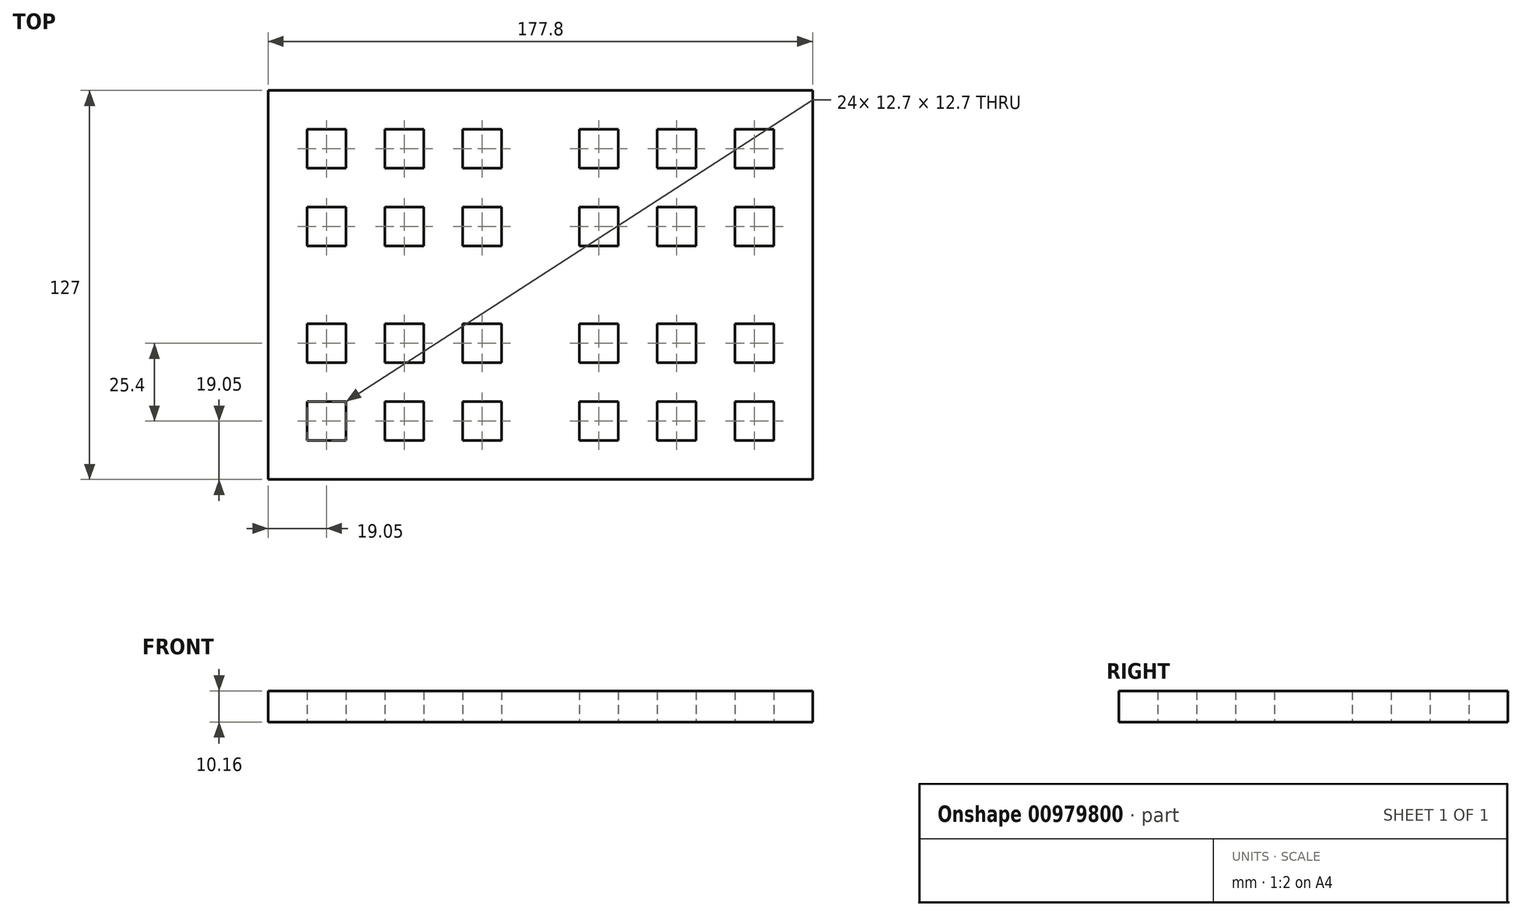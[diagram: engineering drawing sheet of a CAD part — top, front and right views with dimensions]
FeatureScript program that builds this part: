
annotation { "Feature Type Name" : "Feature", "Feature Type Description" : "" }
export const myFeature = defineFeature(function(context is Context, id is Id, definition is map)
    precondition{}
    {
        {
            var Q0;
            Q0=qCreatedBy(makeId("Top.planeOp"),FACE);
            var sketch = newSketch(context, id + "F0", { "sketchPlane" : qUnion([Q0])});
            skLineSegment(sketch, "E0.bottom", {"start": v(-88.9, 63.5) * mm, "end": v(88.9, 63.5) * mm});
            skLineSegment(sketch, "E0.top", {"start": v(-88.9, -63.5) * mm, "end": v(88.9, -63.5) * mm});
            skLineSegment(sketch, "E0.left", {"start": v(-88.9, 63.5) * mm, "end": v(-88.9, -63.5) * mm});
            skLineSegment(sketch, "E0.right", {"start": v(88.9, 63.5) * mm, "end": v(88.9, -63.5) * mm});
            skPoint(sketch, "E0.middle", {"position": v(0, 0) * mm});
            skLineSegment(sketch, "E1.bottom", {"start": v(-50.8, 50.8) * mm, "end": v(-38.1, 50.8) * mm});
            skLineSegment(sketch, "E1.top", {"start": v(-50.8, 38.1) * mm, "end": v(-38.1, 38.1) * mm});
            skLineSegment(sketch, "E1.left", {"start": v(-50.8, 50.8) * mm, "end": v(-50.8, 38.1) * mm});
            skLineSegment(sketch, "E2.2.0.0", {"start": v(-12.7, 50.8) * mm, "end": v(-12.7, 38.1) * mm});
            skLineSegment(sketch, "E2.2.0.1", {"start": v(-25.4, 50.8) * mm, "end": v(-12.7, 50.8) * mm});
            skLineSegment(sketch, "E2.2.0.2", {"start": v(-25.4, 38.1) * mm, "end": v(-12.7, 38.1) * mm});
            skLineSegment(sketch, "E3", {"start": v(-25.4, 50.8) * mm, "end": v(-25.4, 38.1) * mm});
            skLineSegment(sketch, "E4", {"start": v(-38.1, 50.8) * mm, "end": v(-38.1, 38.1) * mm});
            skLineSegment(sketch, "E5.0.1.0", {"start": v(-50.8, 25.4) * mm, "end": v(-38.1, 25.4) * mm});
            skLineSegment(sketch, "E5.0.1.1", {"start": v(-50.8, 25.4) * mm, "end": v(-50.8, 12.7) * mm});
            skLineSegment(sketch, "E5.0.1.2", {"start": v(-38.1, 25.4) * mm, "end": v(-38.1, 12.7) * mm});
            skLineSegment(sketch, "E5.0.1.3", {"start": v(-50.8, 12.7) * mm, "end": v(-38.1, 12.7) * mm});
            skLineSegment(sketch, "E5.0.1.4", {"start": v(-25.4, 25.4) * mm, "end": v(-25.4, 12.7) * mm});
            skLineSegment(sketch, "E5.0.1.5", {"start": v(-25.4, 12.7) * mm, "end": v(-12.7, 12.7) * mm});
            skLineSegment(sketch, "E5.0.1.6", {"start": v(-12.7, 25.4) * mm, "end": v(-12.7, 12.7) * mm});
            skLineSegment(sketch, "E5.0.1.7", {"start": v(-25.4, 25.4) * mm, "end": v(-12.7, 25.4) * mm});
            skLineSegment(sketch, "E5.1.1.4", {"start": v(-50.8, 25.4) * mm, "end": v(-50.8, 12.7) * mm});
            skLineSegment(sketch, "E5.1.1.5", {"start": v(-50.8, 12.7) * mm, "end": v(-38.1, 12.7) * mm});
            skLineSegment(sketch, "E5.1.1.6", {"start": v(-38.1, 25.4) * mm, "end": v(-38.1, 12.7) * mm});
            skLineSegment(sketch, "E5.1.1.7", {"start": v(-50.8, 25.4) * mm, "end": v(-38.1, 25.4) * mm});
            skLineSegment(sketch, "E6.0.1.0", {"start": v(-50.8, -12.7) * mm, "end": v(-38.1, -12.7) * mm});
            skLineSegment(sketch, "E6.0.1.1", {"start": v(-38.1, -12.7) * mm, "end": v(-38.1, -25.4) * mm});
            skLineSegment(sketch, "E6.0.1.2", {"start": v(-50.8, -25.4) * mm, "end": v(-38.1, -25.4) * mm});
            skLineSegment(sketch, "E6.0.1.3", {"start": v(-50.8, -12.7) * mm, "end": v(-50.8, -25.4) * mm});
            skLineSegment(sketch, "E6.0.1.4", {"start": v(-25.4, -12.7) * mm, "end": v(-25.4, -25.4) * mm});
            skLineSegment(sketch, "E6.0.1.5", {"start": v(-25.4, -12.7) * mm, "end": v(-12.7, -12.7) * mm});
            skLineSegment(sketch, "E6.0.1.6", {"start": v(-12.7, -12.7) * mm, "end": v(-12.7, -25.4) * mm});
            skLineSegment(sketch, "E6.0.1.7", {"start": v(-25.4, -25.4) * mm, "end": v(-12.7, -25.4) * mm});
            skLineSegment(sketch, "E6.0.1.8", {"start": v(-25.4, -38.1) * mm, "end": v(-12.7, -38.1) * mm});
            skLineSegment(sketch, "E6.0.1.9", {"start": v(-12.7, -38.1) * mm, "end": v(-12.7, -50.8) * mm});
            skLineSegment(sketch, "E6.0.1.10", {"start": v(-25.4, -50.8) * mm, "end": v(-12.7, -50.8) * mm});
            skLineSegment(sketch, "E6.0.1.11", {"start": v(-25.4, -38.1) * mm, "end": v(-25.4, -50.8) * mm});
            skLineSegment(sketch, "E6.0.1.12", {"start": v(-38.1, -38.1) * mm, "end": v(-38.1, -50.8) * mm});
            skLineSegment(sketch, "E6.0.1.13", {"start": v(-50.8, -50.8) * mm, "end": v(-38.1, -50.8) * mm});
            skLineSegment(sketch, "E6.0.1.14", {"start": v(-50.8, -38.1) * mm, "end": v(-50.8, -50.8) * mm});
            skLineSegment(sketch, "E6.0.1.15", {"start": v(-50.8, -38.1) * mm, "end": v(-38.1, -38.1) * mm});
            skLineSegment(sketch, "E6.1.0.0", {"start": v(12.7, 50.8) * mm, "end": v(25.4, 50.8) * mm});
            skLineSegment(sketch, "E6.1.0.1", {"start": v(25.4, 50.8) * mm, "end": v(25.4, 38.1) * mm});
            skLineSegment(sketch, "E6.1.0.2", {"start": v(12.7, 38.1) * mm, "end": v(25.4, 38.1) * mm});
            skLineSegment(sketch, "E6.1.0.3", {"start": v(12.7, 50.8) * mm, "end": v(12.7, 38.1) * mm});
            skLineSegment(sketch, "E6.1.0.4", {"start": v(38.1, 50.8) * mm, "end": v(38.1, 38.1) * mm});
            skLineSegment(sketch, "E6.1.0.5", {"start": v(38.1, 50.8) * mm, "end": v(50.8, 50.8) * mm});
            skLineSegment(sketch, "E6.1.0.6", {"start": v(50.8, 50.8) * mm, "end": v(50.8, 38.1) * mm});
            skLineSegment(sketch, "E6.1.0.7", {"start": v(38.1, 38.1) * mm, "end": v(50.8, 38.1) * mm});
            skLineSegment(sketch, "E6.1.0.8", {"start": v(38.1, 25.4) * mm, "end": v(50.8, 25.4) * mm});
            skLineSegment(sketch, "E6.1.0.9", {"start": v(50.8, 25.4) * mm, "end": v(50.8, 12.7) * mm});
            skLineSegment(sketch, "E6.1.0.10", {"start": v(38.1, 12.7) * mm, "end": v(50.8, 12.7) * mm});
            skLineSegment(sketch, "E6.1.0.11", {"start": v(38.1, 25.4) * mm, "end": v(38.1, 12.7) * mm});
            skLineSegment(sketch, "E6.1.0.12", {"start": v(25.4, 25.4) * mm, "end": v(25.4, 12.7) * mm});
            skLineSegment(sketch, "E6.1.0.13", {"start": v(12.7, 12.7) * mm, "end": v(25.4, 12.7) * mm});
            skLineSegment(sketch, "E6.1.0.14", {"start": v(12.7, 25.4) * mm, "end": v(12.7, 12.7) * mm});
            skLineSegment(sketch, "E6.1.0.15", {"start": v(12.7, 25.4) * mm, "end": v(25.4, 25.4) * mm});
            skLineSegment(sketch, "E6.1.1.0", {"start": v(12.7, -12.7) * mm, "end": v(25.4, -12.7) * mm});
            skLineSegment(sketch, "E6.1.1.1", {"start": v(25.4, -12.7) * mm, "end": v(25.4, -25.4) * mm});
            skLineSegment(sketch, "E6.1.1.2", {"start": v(12.7, -25.4) * mm, "end": v(25.4, -25.4) * mm});
            skLineSegment(sketch, "E6.1.1.3", {"start": v(12.7, -12.7) * mm, "end": v(12.7, -25.4) * mm});
            skLineSegment(sketch, "E6.1.1.4", {"start": v(38.1, -12.7) * mm, "end": v(38.1, -25.4) * mm});
            skLineSegment(sketch, "E6.1.1.5", {"start": v(38.1, -12.7) * mm, "end": v(50.8, -12.7) * mm});
            skLineSegment(sketch, "E6.1.1.6", {"start": v(50.8, -12.7) * mm, "end": v(50.8, -25.4) * mm});
            skLineSegment(sketch, "E6.1.1.7", {"start": v(38.1, -25.4) * mm, "end": v(50.8, -25.4) * mm});
            skLineSegment(sketch, "E6.1.1.8", {"start": v(38.1, -38.1) * mm, "end": v(50.8, -38.1) * mm});
            skLineSegment(sketch, "E6.1.1.9", {"start": v(50.8, -38.1) * mm, "end": v(50.8, -50.8) * mm});
            skLineSegment(sketch, "E6.1.1.10", {"start": v(38.1, -50.8) * mm, "end": v(50.8, -50.8) * mm});
            skLineSegment(sketch, "E6.1.1.11", {"start": v(38.1, -38.1) * mm, "end": v(38.1, -50.8) * mm});
            skLineSegment(sketch, "E6.1.1.12", {"start": v(25.4, -38.1) * mm, "end": v(25.4, -50.8) * mm});
            skLineSegment(sketch, "E6.1.1.13", {"start": v(12.7, -50.8) * mm, "end": v(25.4, -50.8) * mm});
            skLineSegment(sketch, "E6.1.1.14", {"start": v(12.7, -38.1) * mm, "end": v(12.7, -50.8) * mm});
            skLineSegment(sketch, "E6.1.1.15", {"start": v(12.7, -38.1) * mm, "end": v(25.4, -38.1) * mm});
            skLineSegment(sketch, "E7.1.0.0", {"start": v(-76.2, 12.7) * mm, "end": v(-63.5, 12.7) * mm});
            skLineSegment(sketch, "E7.1.0.1", {"start": v(-76.2, 25.4) * mm, "end": v(-76.2, 12.7) * mm});
            skLineSegment(sketch, "E7.1.0.2", {"start": v(-63.5, 25.4) * mm, "end": v(-63.5, 12.7) * mm});
            skLineSegment(sketch, "E7.1.0.3", {"start": v(-76.2, 50.8) * mm, "end": v(-63.5, 50.8) * mm});
            skLineSegment(sketch, "E7.1.0.4", {"start": v(-76.2, 50.8) * mm, "end": v(-76.2, 38.1) * mm});
            skLineSegment(sketch, "E7.1.0.5", {"start": v(-63.5, 50.8) * mm, "end": v(-63.5, 38.1) * mm});
            skLineSegment(sketch, "E7.1.0.6", {"start": v(-76.2, 38.1) * mm, "end": v(-63.5, 38.1) * mm});
            skLineSegment(sketch, "E7.1.0.7", {"start": v(-76.2, 25.4) * mm, "end": v(-63.5, 25.4) * mm});
            skLineSegment(sketch, "E7.1.0.8", {"start": v(-76.2, 12.7) * mm, "end": v(-63.5, 12.7) * mm});
            skLineSegment(sketch, "E7.1.0.9", {"start": v(-76.2, 50.8) * mm, "end": v(-63.5, 50.8) * mm});
            skLineSegment(sketch, "E7.1.0.10", {"start": v(-76.2, 38.1) * mm, "end": v(-63.5, 38.1) * mm});
            skLineSegment(sketch, "E7.1.0.11", {"start": v(-76.2, 50.8) * mm, "end": v(-76.2, 38.1) * mm});
            skLineSegment(sketch, "E7.1.0.12", {"start": v(-63.5, 25.4) * mm, "end": v(-63.5, 12.7) * mm});
            skLineSegment(sketch, "E7.1.0.13", {"start": v(-76.2, 25.4) * mm, "end": v(-76.2, 12.7) * mm});
            skLineSegment(sketch, "E7.1.0.14", {"start": v(-63.5, 50.8) * mm, "end": v(-63.5, 38.1) * mm});
            skLineSegment(sketch, "E7.1.0.15", {"start": v(-76.2, 25.4) * mm, "end": v(-63.5, 25.4) * mm});
            skLineSegment(sketch, "E8.1.0.0", {"start": v(-76.2, -50.8) * mm, "end": v(-63.5, -50.8) * mm});
            skLineSegment(sketch, "E8.1.0.1", {"start": v(-76.2, -38.1) * mm, "end": v(-76.2, -50.8) * mm});
            skLineSegment(sketch, "E8.1.0.2", {"start": v(-63.5, -38.1) * mm, "end": v(-63.5, -50.8) * mm});
            skLineSegment(sketch, "E8.1.0.3", {"start": v(-76.2, -12.7) * mm, "end": v(-63.5, -12.7) * mm});
            skLineSegment(sketch, "E8.1.0.4", {"start": v(-76.2, -12.7) * mm, "end": v(-76.2, -25.4) * mm});
            skLineSegment(sketch, "E8.1.0.5", {"start": v(-63.5, -12.7) * mm, "end": v(-63.5, -25.4) * mm});
            skLineSegment(sketch, "E8.1.0.6", {"start": v(-76.2, -25.4) * mm, "end": v(-63.5, -25.4) * mm});
            skLineSegment(sketch, "E8.1.0.7", {"start": v(-76.2, -38.1) * mm, "end": v(-63.5, -38.1) * mm});
            skLineSegment(sketch, "E8.1.0.8", {"start": v(-76.2, -50.8) * mm, "end": v(-63.5, -50.8) * mm});
            skLineSegment(sketch, "E8.1.0.9", {"start": v(-76.2, -12.7) * mm, "end": v(-63.5, -12.7) * mm});
            skLineSegment(sketch, "E8.1.0.10", {"start": v(-76.2, -25.4) * mm, "end": v(-63.5, -25.4) * mm});
            skLineSegment(sketch, "E8.1.0.11", {"start": v(-76.2, -12.7) * mm, "end": v(-76.2, -25.4) * mm});
            skLineSegment(sketch, "E8.1.0.12", {"start": v(-63.5, -38.1) * mm, "end": v(-63.5, -50.8) * mm});
            skLineSegment(sketch, "E8.1.0.13", {"start": v(-76.2, -38.1) * mm, "end": v(-76.2, -50.8) * mm});
            skLineSegment(sketch, "E8.1.0.14", {"start": v(-63.5, -12.7) * mm, "end": v(-63.5, -25.4) * mm});
            skLineSegment(sketch, "E8.1.0.15", {"start": v(-76.2, -38.1) * mm, "end": v(-63.5, -38.1) * mm});
            skLineSegment(sketch, "E9.1.0.4", {"start": v(63.52, 50.8) * mm, "end": v(63.52, 38.1) * mm});
            skLineSegment(sketch, "E9.1.0.5", {"start": v(63.52, 50.8) * mm, "end": v(76.22, 50.8) * mm});
            skLineSegment(sketch, "E9.1.0.6", {"start": v(76.22, 50.8) * mm, "end": v(76.22, 38.1) * mm});
            skLineSegment(sketch, "E9.1.0.7", {"start": v(63.52, 38.1) * mm, "end": v(76.22, 38.1) * mm});
            skLineSegment(sketch, "E9.1.0.8", {"start": v(63.52, 25.4) * mm, "end": v(76.22, 25.4) * mm});
            skLineSegment(sketch, "E9.1.0.9", {"start": v(76.22, 25.4) * mm, "end": v(76.22, 12.7) * mm});
            skLineSegment(sketch, "E9.1.0.10", {"start": v(63.52, 12.7) * mm, "end": v(76.22, 12.7) * mm});
            skLineSegment(sketch, "E9.1.0.11", {"start": v(63.52, 25.4) * mm, "end": v(63.52, 12.7) * mm});
            skLineSegment(sketch, "E9.1.1.4", {"start": v(63.52, -12.7) * mm, "end": v(63.52, -25.4) * mm});
            skLineSegment(sketch, "E9.1.1.5", {"start": v(63.52, -12.7) * mm, "end": v(76.22, -12.7) * mm});
            skLineSegment(sketch, "E9.1.1.6", {"start": v(76.22, -12.7) * mm, "end": v(76.22, -25.4) * mm});
            skLineSegment(sketch, "E9.1.1.7", {"start": v(63.52, -25.4) * mm, "end": v(76.22, -25.4) * mm});
            skLineSegment(sketch, "E9.1.1.8", {"start": v(63.52, -38.1) * mm, "end": v(76.22, -38.1) * mm});
            skLineSegment(sketch, "E9.1.1.9", {"start": v(76.22, -38.1) * mm, "end": v(76.22, -50.8) * mm});
            skLineSegment(sketch, "E9.1.1.10", {"start": v(63.52, -50.8) * mm, "end": v(76.22, -50.8) * mm});
            skLineSegment(sketch, "E9.1.1.11", {"start": v(63.52, -38.1) * mm, "end": v(63.52, -50.8) * mm});
            skSolve(sketch);
        }
        {
            var Q0;
            Q0 = qSketchRegion(id + "F0", true);
            extrude(context, id + "F1", {"entities" : qUnion([Q0]), "depth" : 10.16 * mm, "offsetDistance" : 25.4 * mm});
        }
    });
